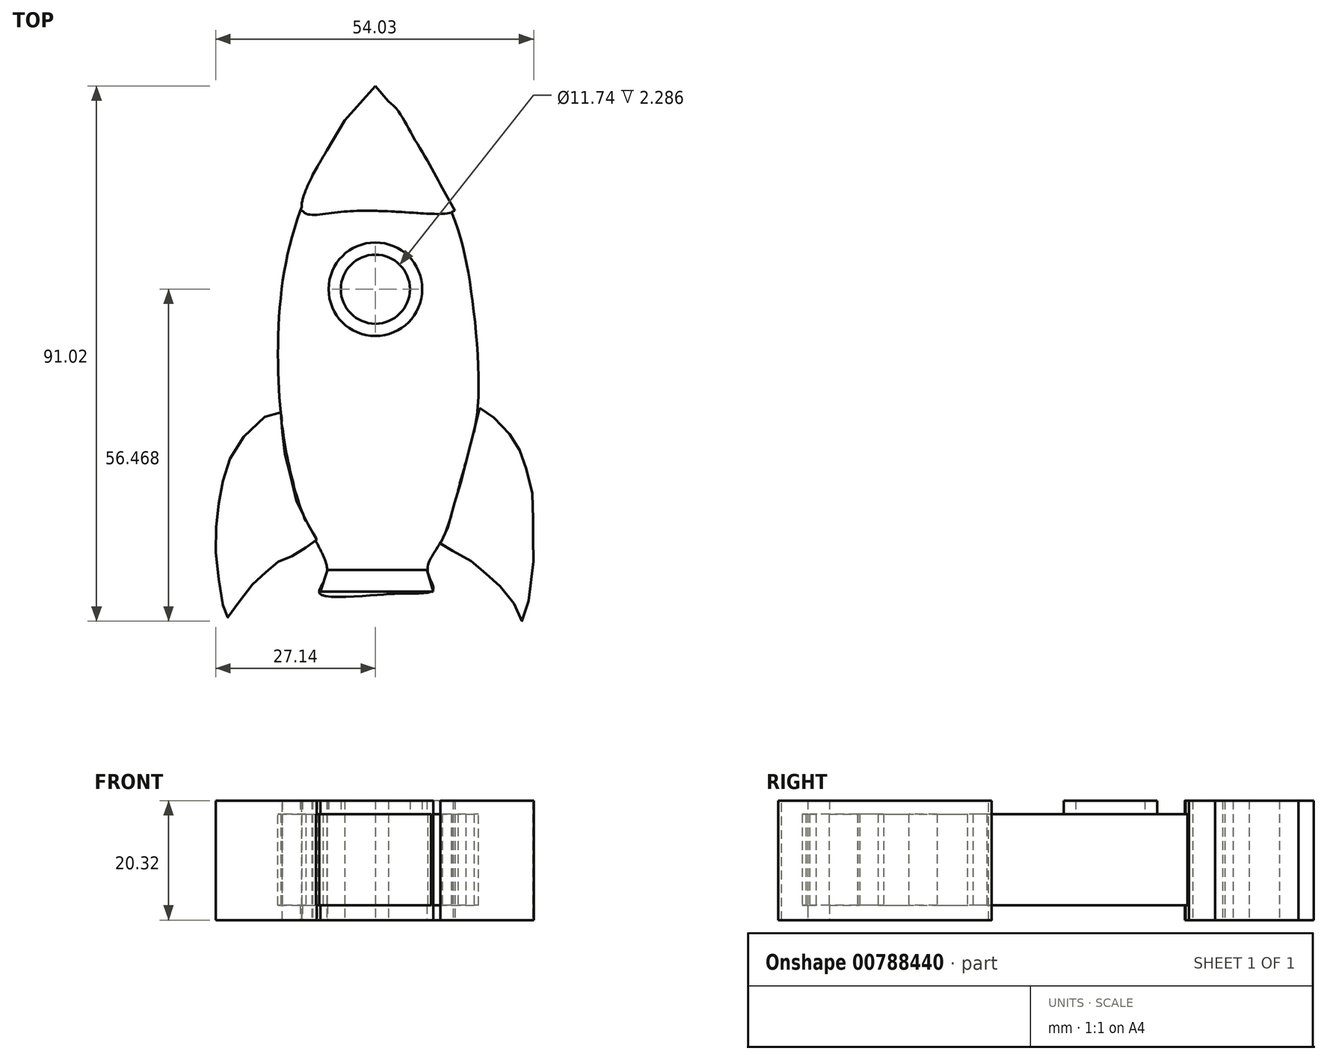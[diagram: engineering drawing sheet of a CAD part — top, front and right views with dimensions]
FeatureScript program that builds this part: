
annotation { "Feature Type Name" : "Feature", "Feature Type Description" : "" }
export const myFeature = defineFeature(function(context is Context, id is Id, definition is map)
    precondition{}
    {
        {
            var Q0;
            Q0=qCreatedBy(makeId("Top.planeOp"),FACE);
            var sketch = newSketch(context, id + "F0", { "sketchPlane" : qUnion([Q0])});
            skFitSpline(sketch, "E0", {"points": [v(-10.38, -25.42) * mm, v(-13.08, -19.1) * mm, v(-15.19, -10.38) * mm, v(-16.4, 0) * mm, v(-16.1, 15.5) * mm, v(-12.78, 30.23) * mm, v(-5.56, 44.67) * mm, v(0, 49.48) * mm, v(4.66, 45.27) * mm, v(12.78, 30.53) * mm, v(16.4, 15.8) * mm, v(17.3, -4.06) * mm, v(14.59, -15.19) * mm, v(11.28, -25.72) * mm, v(8.87, -30.83) * mm, v(9.78, -34.14) * mm, v(6.17, -34.74) * mm, v(0, -35.04) * mm, v(-9.47, -34.74) * mm, v(-8.27, -31.73) * mm, v(-10.38, -25.42) * mm]});
            skSolve(sketch);
        }
        {
            var Q0;
            Q0=qSketchRegion(id+"F0",true);
            extrude(context, id + "F1", {"entities" : qUnion([Q0]), "depth" : 15.5 * mm, "offsetDistance" : 25.4 * mm});
        }
        {
            var Q0;
            Q0=qCreatedBy(makeId("Top.planeOp"),FACE);
            var sketch = newSketch(context, id + "F2", { "sketchPlane" : qUnion([Q0])});
            skFitSpline(sketch, "E1", {"points": [v(-12.4, 30.4) * mm, v(-6.68, 30.03) * mm, v(5.48, 30.03) * mm, v(13.17, 30.21) * mm, v(12.64, 31.82) * mm, v(9.78, 37.19) * mm, v(6.02, 43.63) * mm, v(3.16, 48.1) * mm, v(0, 49.53) * mm, v(-3.46, 47.38) * mm, v(-7.57, 41.66) * mm, v(-12.4, 30.4) * mm]});
            skSolve(sketch);
        }
        {
            var Q0;
            Q0=qSketchRegion(id+"F2",true);
            extrude(context, id + "F3", {"entities" : qUnion([Q0]), "operationType" : NewBodyOperationType.ADD, "depth" : 17.78 * mm, "offsetDistance" : 25.4 * mm, "hasSecondDirection" : true, "secondDirectionOppositeDirection" : true, "secondDirectionDepth" : 2.54 * mm});
        }
        {
            var Q0;
            Q0=qCreatedBy(makeId("Top.planeOp"),FACE);
            var sketch = newSketch(context, id + "F4", { "sketchPlane" : qUnion([Q0])});
            skCircle(sketch, "E2", {"center": v(0, 16.98) * mm, "radius": 7.95 * mm});
            skCircle(sketch, "E3", {"center": v(0, 16.98) * mm, "radius": 5.87 * mm});
            skSolve(sketch);
        }
        {
            var Q0;
            Q0=qSketchRegion(id+"F4",true);
            extrude(context, id + "F5", {"entities" : qUnion([Q0]), "operationType" : NewBodyOperationType.ADD, "depth" : 17.78 * mm, "offsetDistance" : 25.4 * mm});
        }
        {
            var Q0;
            Q0=qCreatedBy(makeId("Top.planeOp"),FACE);
            var sketch = newSketch(context, id + "F6", { "sketchPlane" : qUnion([Q0])});
            skFitSpline(sketch, "E4", {"points": [v(-9.97, -25.63) * mm, v(-11.62, -26.84) * mm, v(-14.33, -28.5) * mm, v(-16.74, -29.54) * mm, v(-19.3, -31.8) * mm, v(-22.45, -35.1) * mm, v(-25.16, -38.87) * mm, v(-26.06, -35.86) * mm, v(-27.12, -27.29) * mm, v(-26.66, -20.07) * mm, v(-25.46, -13.9) * mm, v(-21.55, -7.13) * mm, v(-16.29, -3.83) * mm, v(-15.84, -8.19) * mm, v(-14.63, -13.9) * mm, v(-12.38, -21.57) * mm, v(-9.97, -25.63) * mm]});
            skFitSpline(sketch, "E5", {"points": [v(17.7, -3.22) * mm, v(20.4, -5.18) * mm, v(23.72, -8.94) * mm, v(25.22, -12.25) * mm, v(26.73, -18.41) * mm, v(26.73, -24.43) * mm, v(26.88, -28.34) * mm, v(25.07, -39.47) * mm, v(23.72, -36.76) * mm, v(20.56, -33) * mm, v(17.7, -30.45) * mm, v(14.1, -27.89) * mm, v(11.08, -26.54) * mm, v(11.84, -24.73) * mm, v(13.64, -18.56) * mm, v(14.84, -14.8) * mm, v(15.9, -10.3) * mm, v(17.1, -5.78) * mm, v(17.7, -3.22) * mm]});
            skSolve(sketch);
        }
        {
            var Q0;
            Q0=qSketchRegion(id+"F6",true);
            extrude(context, id + "F7", {"entities" : qUnion([Q0]), "operationType" : NewBodyOperationType.ADD, "depth" : 17.78 * mm, "offsetDistance" : 25.4 * mm, "hasSecondDirection" : true, "secondDirectionOppositeDirection" : true, "secondDirectionDepth" : 2.54 * mm});
        }
        {
            var Q0;
            Q0=qCreatedBy(makeId("Top.planeOp"),FACE);
            var sketch = newSketch(context, id + "F8", { "sketchPlane" : qUnion([Q0])});
            skLineSegment(sketch, "E6", {"start": v(-8.15, -30.75) * mm, "end": v(-9.3, -34.44) * mm});
            skLineSegment(sketch, "E7", {"start": v(-9.3, -34.44) * mm, "end": v(9.86, -34.44) * mm});
            skLineSegment(sketch, "E8", {"start": v(9.86, -34.44) * mm, "end": v(8.78, -30.75) * mm});
            skLineSegment(sketch, "E9", {"start": v(8.78, -30.75) * mm, "end": v(-8.15, -30.75) * mm});
            skLineSegment(sketch, "E10", {"start": v(-12.75, 30.3) * mm, "end": v(-10.68, 36.39) * mm});
            skLineSegment(sketch, "E11", {"start": v(-10.68, 36.39) * mm, "end": v(-5.24, 45.7) * mm});
            skLineSegment(sketch, "E12", {"start": v(-5.24, 45.7) * mm, "end": v(0, 51.53) * mm});
            skLineSegment(sketch, "E13", {"start": v(0, 51.53) * mm, "end": v(4.85, 45.7) * mm});
            skLineSegment(sketch, "E14", {"start": v(4.85, 45.7) * mm, "end": v(10.16, 36.39) * mm});
            skLineSegment(sketch, "E15", {"start": v(10.16, 36.39) * mm, "end": v(13.53, 30.3) * mm});
            skLineSegment(sketch, "E16", {"start": v(13.53, 30.3) * mm, "end": v(-12.75, 30.3) * mm});
            skSolve(sketch);
        }
        {
            var Q0;
            Q0=qSketchRegion(id+"F8",true);
            extrude(context, id + "F9", {"entities" : qUnion([Q0]), "operationType" : NewBodyOperationType.ADD, "depth" : 17.78 * mm, "offsetDistance" : 25.4 * mm, "hasSecondDirection" : true, "secondDirectionOppositeDirection" : true, "secondDirectionDepth" : 2.54 * mm});
        }
    });
